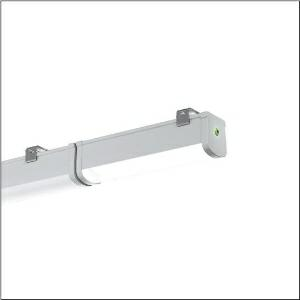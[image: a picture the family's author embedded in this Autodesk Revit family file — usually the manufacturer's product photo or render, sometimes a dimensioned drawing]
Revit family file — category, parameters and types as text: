
# Revit family: monsun_r__31_58fa207a403b3g_c1e4
name_source: partatom
category: Lighting Fixtures
units: mm (PartAtom-declared; Revit-internal decimal feet)

## family parameters
Cut with Voids When Loaded = No
Host = Face
Light Source = No
Part Type = Normal
Room Calculation Point = No
Round Connector Dimension = Use Diameter
Shared = No

## types (1)
- --- (1 x LED, 450 lm, 5 W, 4000K)
    Apparent Load = 5 VA
    CIE Flux Codes = 42 72 91 92 100
    Color Rendering = 80
    Color Temperature = 4000K
    Default Elevation = 1800 mm
    Description = Monsun® 31, emergency light element, primary optical cover: diffuser, of PC, frosted, light emission: direct distribution, primary light characteristic: symmetric, installation type: surface-mounted, EM-KIT 3h,LED, rated luminous flux: 450lm, luminous efficacy: 100lm/W, light colour: 840, colour temperature: 4000K, control gear: without control gear, emergency light function, with socket/plug, mains connection: 220..240V, AC, 50..60Hz, rated input power: 5W, housing, luminaire housing, of PC, light grey (RAL 7035), length: 297mm, width: 68mm, height: 76mm, protection rating (complete): IP65, insulation class (complete): insulation class II (safety insulation), certification: CE, protection symbol: D, impact resistance: IK08, permissible operating ambient temperature: 0..+40°C, standard: EN 60598-2-22, corresponds to IFS (International Featured Standards) requirements for safety and quality in the food industry, packaging unit: 1 piece
    Height = 77 mm
    Lamp = 1 x LED
    Lamp Light Flux = 450 lm
    Lamp Power = 5 W
    Lamp count = 1
    Length = 294 mm
    Luminous efficacy = 90 lm/W
    Manufacturer = Siteco
    ModVariant = No
    Model = 58FA207A403B3G
    Mounting Place = Ceiling
    Mounting Type = Surface mounted
    Number of Poles = 1
    OnlyDefault = Yes
    Power Factor = 1
    Product Name = Monsun® 31
    Product group = emergency light element
    ProductGroupID = 305
    Protection Class = Protection class II
    Protection Degree = IP 65
    RLX_Detail_Level = 1
    RlxData = <blob elided: 31193 chars, md5=492f2bd7>
    Socket = socket
    Standby Power = 0 W
    System Light Flux = 450 lm
    System Power = 5 W
    Type Comments = : 3 h
    Type Image = l_1006658.jpg
    URL = http://relux.com
    VarID = @adj_129869
    Voltage = 0 V
    Weight = 0.00 kg
    Width = 69 mm

## geometry (parser evidence)
native form markers: Blend x4, Sweep x14
no freeform markers — native parametric forms only
